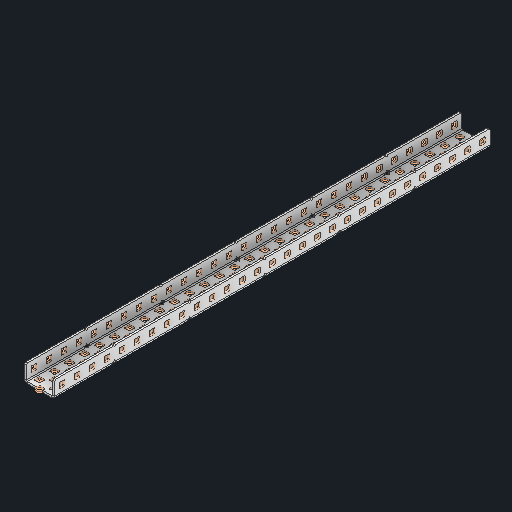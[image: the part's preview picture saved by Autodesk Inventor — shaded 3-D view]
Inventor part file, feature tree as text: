
AUTODESK INVENTOR PART (.ipt)
format: ipt  version: 2025 (Build 290162000, 162)  size: 2,317,312 bytes
history: native  units: in
note: dims shown in document units (in); Inventor stores cm internally (conversion verified against a paired STEP export)
features: other x296, sketch x5, sheet_metal_op x1
ambient origin geometry x8: Origin, YZ Plane, XZ Plane, XY Plane, X Axis, Y Axis, Z Axis, Center Point
bodies: Solid1 (feature_tree)
feature tree (302):
  other  "Alu C 1x2x1x29.ipt"
  other  "Solid1::Alu C 1x2x1x29.ipt"
  other  "TaggingFeature1"
  sketch  "Sketch1"  dims[d0=0.3937in]
  sketch  "Sketch2"  dims[d1=0.0625in]
  sketch  "Sketch3"
  other  "Flange Pattern Sketch"
  sketch  "Sketch9"
  sheet_metal_op  "Body Pattern Sketch"
  other  "Arc Length"
  sketch  "Sketch14"
  other  "Flange Pattern Plane"
  other  "Srf1"
  other  "Srf2"
  other  "Srf3"
  other  "Srf4"
  other  "Srf5"
  other  "Srf6"
  other  "Srf7"
  other  "Srf8"
  other  "Srf9"
  other  "Srf10"
  other  "Srf11"
  other  "Srf12"
  other  "Srf13"
  other  "Srf14"
  other  "Srf15"
  other  "Srf16"
  other  "Srf17"
  other  "Srf18"
  other  "Srf19"
  other  "Srf20"
  other  "Srf21"
  other  "Srf22"
  other  "Srf23"
  other  "Srf24"
  other  "Srf25"
  other  "Srf26"
  other  "Srf27"
  other  "Srf28"
  other  "Srf29"
  other  "Srf30"
  other  "Srf31"
  other  "Srf32"
  other  "Srf33"
  other  "Srf34"
  other  "Srf35"
  other  "Srf36"
  other  "Srf37"
  other  "Srf38"
  other  "Srf39"
  other  "Srf40"
  other  "Srf41"
  other  "Srf42"
  other  "Srf43"
  other  "Srf44"
  other  "Srf45"
  other  "Srf46"
  other  "Srf47"
  other  "Srf48"
  other  "Srf49"
  other  "Srf50"
  other  "Srf51"
  other  "Srf52"
  other  "Srf53"
  other  "Srf54"
  other  "Srf55"
  other  "Srf56"
  other  "Srf57"
  other  "Srf58"
  other  "Srf59"
  other  "Srf60"
  other  "Srf61"
  other  "Srf62"
  other  "Srf63"
  other  "Srf64"
  other  "Srf65"
  other  "Srf66"
  other  "Srf67"
  other  "Srf68"
  other  "Srf69"
  other  "Srf70"
  other  "Srf71"
  other  "Srf72"
  other  "Srf73"
  other  "Srf74"
  other  "Srf75"
  other  "Srf76"
  other  "Srf77"
  other  "Srf78"
  other  "Srf79"
  other  "Srf80"
  other  "Srf81"
  other  "Srf82"
  other  "Srf83"
  other  "Srf84"
  other  "Srf85"
  other  "Srf86"
  other  "Srf87"
  other  "Srf88"
  other  "Srf89"
  other  "Srf90"
  other  "Srf91"
  other  "Srf92"
  other  "Srf93"
  other  "Srf94"
  other  "Srf95"
  other  "Srf96"
  other  "Srf97"
  other  "Srf98"
  other  "Srf99"
  other  "Srf100"
  other  "Srf101"
  other  "Srf102"
  other  "Srf103"
  other  "Srf104"
  other  "Srf105"
  other  "Srf106"
  other  "Srf107"
  other  "Srf108"
  other  "Srf109"
  other  "Srf110"
  other  "Srf111"
  other  "Srf112"
  other  "Srf113"
  other  "Srf114"
  other  "Srf115"
  other  "Srf116"
  other  "Srf117"
  other  "Srf118"
  other  "Srf119"
  other  "Srf120"
  other  "Srf121"
  other  "Srf122"
  other  "Srf123"
  other  "Srf124"
  other  "Srf125"
  other  "Srf126"
  other  "Srf127"
  other  "Srf128"
  other  "Srf129"
  other  "Srf130"
  other  "Srf131"
  other  "Srf132"
  other  "Srf133"
  other  "Srf134"
  other  "Srf135"
  other  "Srf136"
  other  "Srf137"
  other  "Srf138"
  other  "Srf139"
  other  "Srf140"
  other  "Srf141"
  other  "Srf142"
  other  "Srf143"
  other  "Srf144"
  other  "Srf145"
  other  "Srf1::Derived"
  other  "Srf2::Derived"
  other  "Srf823::Derived"
  other  "Srf824::Derived"
  other  "Srf825::Derived"
  other  "Srf826::Derived"
  other  "Srf827::Derived"
  other  "Srf828::Derived"
  other  "Srf829::Derived"
  other  "Srf922::Derived"
  other  "Srf923::Derived"
  other  "Srf924::Derived"
  other  "Srf925::Derived"
  other  "Srf926::Derived"
  other  "Srf1143::Derived"
  other  "Srf1144::Derived"
  other  "Srf1145::Derived"
  other  "Srf1146::Derived"
  other  "Srf1147::Derived"
  other  "Srf1148::Derived"
  other  "Srf1149::Derived"
  other  "Srf1150::Derived"
  other  "Srf1151::Derived"
  other  "Srf1152::Derived"
  other  "Srf1153::Derived"
  other  "Srf1154::Derived"
  other  "Srf1155::Derived"
  other  "Srf1156::Derived"
  other  "Srf1157::Derived"
  other  "Srf1158::Derived"
  other  "Srf1159::Derived"
  other  "Srf1160::Derived"
  other  "Srf1161::Derived"
  other  "Srf1162::Derived"
  other  "Srf1163::Derived"
  other  "Srf1164::Derived"
  other  "Srf1165::Derived"
  other  "Srf1166::Derived"
  other  "Srf1167::Derived"
  other  "Srf1168::Derived"
  other  "Srf1169::Derived"
  other  "Srf1170::Derived"
  other  "Srf1171::Derived"
  other  "Srf1172::Derived"
  other  "Srf1173::Derived"
  other  "Srf1174::Derived"
  other  "Srf1175::Derived"
  other  "Srf1176::Derived"
  other  "Srf1177::Derived"
  other  "Srf1178::Derived"
  other  "Srf1179::Derived"
  other  "Srf1180::Derived"
  other  "Srf1181::Derived"
  other  "Srf1182::Derived"
  other  "Srf1183::Derived"
  other  "Srf1184::Derived"
  other  "Srf1185::Derived"
  other  "Srf1186::Derived"
  other  "Srf91::Derived"
  other  "Srf92::Derived"
  other  "Srf856::Derived"
  other  "Srf857::Derived"
  other  "Srf858::Derived"
  other  "Srf859::Derived"
  other  "Srf860::Derived"
  other  "Srf861::Derived"
  other  "Srf862::Derived"
  other  "Srf959::Derived"
  other  "Srf960::Derived"
  other  "Srf961::Derived"
  other  "Srf962::Derived"
  other  "Srf963::Derived"
  other  "Srf1199::Derived"
  other  "Srf1200::Derived"
  other  "Srf1201::Derived"
  other  "Srf1202::Derived"
  other  "Srf1203::Derived"
  other  "Srf1204::Derived"
  other  "Srf1205::Derived"
  other  "Srf1206::Derived"
  other  "Srf1207::Derived"
  other  "Srf1208::Derived"
  other  "Srf1209::Derived"
  other  "Srf1210::Derived"
  other  "Srf1211::Derived"
  other  "Srf1212::Derived"
  other  "Srf1213::Derived"
  other  "Srf1214::Derived"
  other  "Srf1215::Derived"
  other  "Srf1216::Derived"
  other  "Srf1217::Derived"
  other  "Srf1218::Derived"
  other  "Srf1219::Derived"
  other  "Srf1220::Derived"
  other  "Srf1221::Derived"
  other  "Srf1222::Derived"
  other  "Srf1223::Derived"
  other  "Srf1224::Derived"
  other  "Srf1225::Derived"
  other  "Srf1226::Derived"
  other  "Srf1227::Derived"
  other  "Srf1228::Derived"
  other  "Srf1229::Derived"
  other  "Srf1230::Derived"
  other  "Srf1231::Derived"
  other  "Srf1232::Derived"
  other  "Srf1233::Derived"
  other  "Srf1234::Derived"
  other  "Srf1235::Derived"
  other  "Srf1236::Derived"
  other  "Srf1237::Derived"
  other  "Srf1238::Derived"
  other  "Srf1239::Derived"
  other  "Srf1240::Derived"
  other  "Srf1241::Derived"
  other  "Srf1242::Derived"
  other  "Srf786::Derived"
  other  "Srf889::Derived"
  other  "Srf890::Derived"
  other  "Srf891::Derived"
  other  "Srf892::Derived"
  other  "Srf893::Derived"
  other  "Srf894::Derived"
  other  "Srf895::Derived"
  other  "Srf896::Derived"
  other  "Srf996::Derived"
  other  "Srf997::Derived"
  other  "Srf998::Derived"
  other  "Srf999::Derived"
  other  "Srf1000::Derived"
  other  "Srf1255::Derived"
  other  "Srf1256::Derived"
  other  "Srf1257::Derived"
  other  "Srf1258::Derived"
  other  "Srf1259::Derived"
  other  "Srf1260::Derived"
  other  "Srf1261::Derived"
  other  "Srf1262::Derived"
  other  "Srf1263::Derived"
  other  "Srf1264::Derived"
  other  "Srf1265::Derived"
  other  "Srf1266::Derived"
  other  "Srf1267::Derived"
  other  "Srf1268::Derived"
  other  "Srf1269::Derived"
